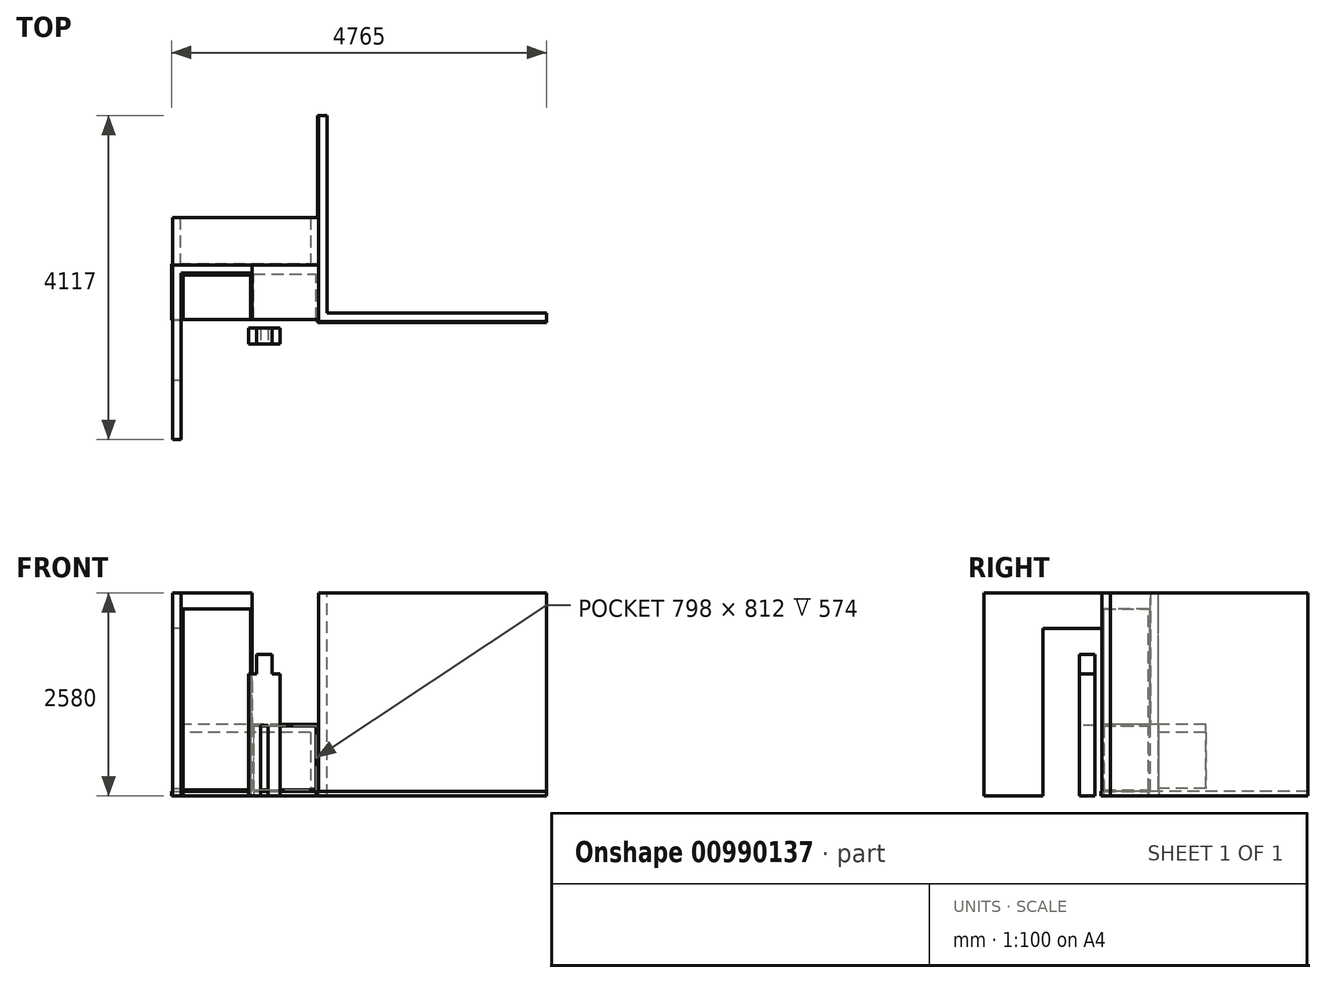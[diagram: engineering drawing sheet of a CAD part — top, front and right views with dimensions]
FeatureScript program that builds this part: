
annotation { "Feature Type Name" : "Feature", "Feature Type Description" : "" }
export const myFeature = defineFeature(function(context is Context, id is Id, definition is map)
    precondition{}
    {
        {
            assignVariable(context, id + "F0", {"name" : "mdf_espessura", "anyValue" : 18 * mm});
        }
        {
            assignVariable(context, id + "F1", {"name" : "porta_largura", "anyValue" : 775 * mm});
        }
        {
            assignVariable(context, id + "F2", {"name" : "parede_entrada_espessura", "anyValue" : 110 * mm});
        }
        {
            assignVariable(context, id + "F3", {"name" : "parede_entrada_largura", "anyValue" : 592 * mm});
        }
        {
            assignVariable(context, id + "F4", {"name" : "parede_janela_largura", "anyValue" : 1745 * mm});
        }
        {
            assignVariable(context, id + "F5", {"name" : "parede_lavanderia_largura", "anyValue" : 620 * mm});
        }
        {
            assignVariable(context, id + "F6", {"name" : "parede_geladeira_largura", "anyValue" : 750 * mm});
        }
        {
            var Q0;
            Q0=qCreatedBy(makeId("Front.planeOp"),FACE);
            var sketch = newSketch(context, id + "F7", { "sketchPlane" : qUnion([Q0])});
            skLineSegment(sketch, "E0.bottom", {"start": v(0, 0) * mm, "end": v(-110, 0) * mm});
            skLineSegment(sketch, "E0.top", {"start": v(0, 2580) * mm, "end": v(-110, 2580) * mm});
            skLineSegment(sketch, "E0.left", {"start": v(0, 0) * mm, "end": v(0, 2580) * mm});
            skLineSegment(sketch, "E0.right", {"start": v(-110, 0) * mm, "end": v(-110, 2580) * mm});
            skSolve(sketch);
        }
        {
            var Q0;
            Q0 = qSketchRegion(id + "F7", true);
            extrude(context, id + "F8", {"entities" : qUnion([Q0]), "depth" : getVariable(context, 'parede_entrada_largura'), "offsetDistance" : 25 * mm});
        }
        {
            var Q0;
            Q0=makeQuery(id+"F8.opExtrude","SWEPT_FACE",FACE,{"disambiguationData":[OSD([sQuery(id+"F7.wireOp",EDGE,"E0.left")])]});
            var sketch = newSketch(context, id + "F9", { "sketchPlane" : qUnion([Q0])});
            skLineSegment(sketch, "E1.bottom", {"start": v(0, 2580) * mm, "end": v(102, 2580) * mm});
            skLineSegment(sketch, "E1.top", {"start": v(0, 0) * mm, "end": v(102, 0) * mm});
            skLineSegment(sketch, "E1.left", {"start": v(0, 2580) * mm, "end": v(0, 0) * mm});
            skLineSegment(sketch, "E1.right", {"start": v(102, 2580) * mm, "end": v(102, 0) * mm});
            skSolve(sketch);
        }
        {
            var Q0;
            Q0 = qSketchRegion(id + "F9", true);
            var Q1;
            Q1=makeQuery(id+"F8.opExtrude","SWEPT_FACE",FACE,{"disambiguationData":[OSD([sQuery(id+"F7.wireOp",EDGE,"E0.right")])]});
            extrude(context, id + "F10", {"entities" : qUnion([Q0]), "operationType" : NewBodyOperationType.ADD, "depth" : getVariable(context, 'parede_janela_largura'), "offsetDistance" : 25 * mm, "hasSecondDirection" : true, "secondDirectionBound" : SecondDirectionBoundingType.UP_TO_SURFACE, "secondDirectionOppositeDirection" : true, "secondDirectionDepth" : 25 * mm, "secondDirectionBoundEntityFace" : qUnion([Q1])});
        }
        {
            var Q0;
            Q0=makeQuery(id+"F10.opExtrude","SWEPT_FACE",FACE,{"disambiguationData":[OSD([sQuery(id+"F9.wireOp",EDGE,"E1.left")])]});
            var sketch = newSketch(context, id + "F11", { "sketchPlane" : qUnion([Q0])});
            skLineSegment(sketch, "E2.bottom", {"start": v(1745, 2580) * mm, "end": v(901, 2580) * mm});
            skLineSegment(sketch, "E2.top", {"start": v(1745, 890) * mm, "end": v(901, 890) * mm});
            skLineSegment(sketch, "E2.left", {"start": v(1745, 2580) * mm, "end": v(1745, 890) * mm});
            skLineSegment(sketch, "E2.right", {"start": v(901, 2580) * mm, "end": v(901, 890) * mm});
            skSolve(sketch);
        }
        {
            var Q0;
            Q0 = qSketchRegion(id + "F11", true);
            extrude(context, id + "F12", {"entities" : qUnion([Q0]), "operationType" : NewBodyOperationType.REMOVE, "endBound" : BoundingType.THROUGH_ALL, "oppositeDirection" : true, "depth" : 25 * mm, "offsetDistance" : 25 * mm});
        }
        {
            var Q0;
            Q0=makeQuery(id+"F10.opExtrude","SWEPT_FACE",FACE,{"disambiguationData":[OSD([sQuery(id+"F9.wireOp",EDGE,"E1.left")])]});
            var sketch = newSketch(context, id + "F13", { "sketchPlane" : qUnion([Q0])});
            skLineSegment(sketch, "E3.bottom", {"start": v(1745, 0) * mm, "end": v(1855, 0) * mm});
            skLineSegment(sketch, "E3.top", {"start": v(1745, 2580) * mm, "end": v(1855, 2580) * mm});
            skLineSegment(sketch, "E3.left", {"start": v(1745, 0) * mm, "end": v(1745, 2580) * mm});
            skLineSegment(sketch, "E3.right", {"start": v(1855, 0) * mm, "end": v(1855, 2580) * mm});
            skSolve(sketch);
        }
        {
            var Q0;
            Q0 = qSketchRegion(id + "F13", true);
            var Q1;
            Q1=makeQuery(id+"F10.opExtrude","SWEPT_FACE",FACE,{"disambiguationData":[OSD([sQuery(id+"F9.wireOp",EDGE,"E1.right")])]});
            extrude(context, id + "F14", {"entities" : qUnion([Q0]), "operationType" : NewBodyOperationType.ADD, "depth" : getVariable(context, 'parede_lavanderia_largura'), "offsetDistance" : 25 * mm, "hasSecondDirection" : true, "secondDirectionOppositeDirection" : true, "secondDirectionDepth" : 2000 * mm, "secondDirectionBoundEntityFace" : qUnion([Q1])});
        }
        {
            var Q0;
            Q0=qCreatedBy(makeId("Top.planeOp"),FACE);
            var sketch = newSketch(context, id + "F15", { "sketchPlane" : qUnion([Q0])});
            skLineSegment(sketch, "E4.bottom", {"start": v(857.83, -903.42) * mm, "end": v(1257.83, -903.42) * mm});
            skLineSegment(sketch, "E4.top", {"start": v(857.83, -703.42) * mm, "end": v(1257.83, -703.42) * mm});
            skLineSegment(sketch, "E4.left", {"start": v(857.83, -903.42) * mm, "end": v(857.83, -703.42) * mm});
            skLineSegment(sketch, "E4.right", {"start": v(1257.83, -903.42) * mm, "end": v(1257.83, -703.42) * mm});
            skSolve(sketch);
        }
        {
            var Q0;
            Q0 = qSketchRegion(id + "F15", true);
            extrude(context, id + "F16", {"entities" : qUnion([Q0]), "depth" : 1550 * mm, "offsetDistance" : 25 * mm});
        }
        {
            var Q0;
            Q0=makeQuery(id+"F16.opExtrude","CAP_FACE",FACE,{"disambiguationData":[OSD([sQuery(id+"F15.wireOp",EDGE,"E4.bottom"),sQuery(id+"F15.wireOp",EDGE,"E4.top"),sQuery(id+"F15.wireOp",EDGE,"E4.left"),sQuery(id+"F15.wireOp",EDGE,"E4.right")])],"isStart":true});
            var sketch = newSketch(context, id + "F17", { "sketchPlane" : qUnion([Q0])});
            skLineSegment(sketch, "E5.bottom", {"start": v(1007.83, 703.42) * mm, "end": v(1107.83, 703.42) * mm});
            skLineSegment(sketch, "E5.top", {"start": v(1007.83, 903.42) * mm, "end": v(1107.83, 903.42) * mm});
            skLineSegment(sketch, "E5.left", {"start": v(1007.83, 703.42) * mm, "end": v(1007.83, 903.42) * mm});
            skLineSegment(sketch, "E5.right", {"start": v(1107.83, 703.42) * mm, "end": v(1107.83, 903.42) * mm});
            skSolve(sketch);
        }
        {
            var Q0;
            Q0 = qSketchRegion(id + "F17", true);
            extrude(context, id + "F18", {"entities" : qUnion([Q0]), "operationType" : NewBodyOperationType.REMOVE, "oppositeDirection" : true, "depth" : 900 * mm, "offsetDistance" : 25 * mm});
        }
        {
            var Q0;
            Q0=makeQuery(id+"F16.opExtrude","CAP_FACE",FACE,{"disambiguationData":[OSD([sQuery(id+"F15.wireOp",EDGE,"E4.bottom"),sQuery(id+"F15.wireOp",EDGE,"E4.top"),sQuery(id+"F15.wireOp",EDGE,"E4.left"),sQuery(id+"F15.wireOp",EDGE,"E4.right")])],"isStart":false});
            var sketch = newSketch(context, id + "F19", { "sketchPlane" : qUnion([Q0])});
            skLineSegment(sketch, "E6.bottom", {"start": v(957.83, -903.42) * mm, "end": v(1157.83, -903.42) * mm});
            skLineSegment(sketch, "E6.top", {"start": v(957.83, -703.42) * mm, "end": v(1157.83, -703.42) * mm});
            skLineSegment(sketch, "E6.left", {"start": v(957.83, -903.42) * mm, "end": v(957.83, -703.42) * mm});
            skLineSegment(sketch, "E6.right", {"start": v(1157.83, -903.42) * mm, "end": v(1157.83, -703.42) * mm});
            skSolve(sketch);
        }
        {
            var Q0;
            Q0 = qSketchRegion(id + "F19", true);
            extrude(context, id + "F20", {"entities" : qUnion([Q0]), "operationType" : NewBodyOperationType.ADD, "depth" : 250 * mm, "offsetDistance" : 25 * mm});
        }
        {
            var Q0;
            Q0=makeQuery(id+"F8.opExtrude","CAP_FACE",FACE,{"disambiguationData":[OSD([sQuery(id+"F7.wireOp",EDGE,"E0.bottom"),sQuery(id+"F7.wireOp",EDGE,"E0.top"),sQuery(id+"F7.wireOp",EDGE,"E0.left"),sQuery(id+"F7.wireOp",EDGE,"E0.right")])],"isStart":false});
            var sketch = newSketch(context, id + "F21", { "sketchPlane" : qUnion([Q0])});
            skLineSegment(sketch, "E7.bottom", {"start": v(0, 2580) * mm, "end": v(-110, 2580) * mm});
            skLineSegment(sketch, "E7.top", {"start": v(0, 2130) * mm, "end": v(-110, 2130) * mm});
            skLineSegment(sketch, "E7.left", {"start": v(0, 2580) * mm, "end": v(0, 2130) * mm});
            skLineSegment(sketch, "E7.right", {"start": v(-110, 2580) * mm, "end": v(-110, 2130) * mm});
            skSolve(sketch);
        }
        {
            var Q0;
            Q0 = qSketchRegion(id + "F21", true);
            extrude(context, id + "F22", {"entities" : qUnion([Q0]), "operationType" : NewBodyOperationType.ADD, "depth" : getVariable(context, 'porta_largura'), "offsetDistance" : 25 * mm});
        }
        {
            var Q0;
            Q0=makeQuery(id+"F22.opExtrude","CAP_FACE",FACE,{"disambiguationData":[OSD([sQuery(id+"F21.wireOp",EDGE,"E7.bottom"),sQuery(id+"F21.wireOp",EDGE,"E7.top"),sQuery(id+"F21.wireOp",EDGE,"E7.left"),sQuery(id+"F21.wireOp",EDGE,"E7.right")])],"isStart":false});
            var sketch = newSketch(context, id + "F23", { "sketchPlane" : qUnion([Q0])});
            skLineSegment(sketch, "E8.bottom", {"start": v(-110, 2580) * mm, "end": v(0, 2580) * mm});
            skLineSegment(sketch, "E8.top", {"start": v(-110, 0) * mm, "end": v(0, 0) * mm});
            skLineSegment(sketch, "E8.left", {"start": v(-110, 2580) * mm, "end": v(-110, 0) * mm});
            skLineSegment(sketch, "E8.right", {"start": v(0, 2580) * mm, "end": v(0, 0) * mm});
            skSolve(sketch);
        }
        {
            var Q0;
            Q0 = qSketchRegion(id + "F23", true);
            extrude(context, id + "F24", {"entities" : qUnion([Q0]), "operationType" : NewBodyOperationType.ADD, "depth" : getVariable(context, 'parede_geladeira_largura'), "offsetDistance" : 25 * mm});
        }
        {
            var Q0;
            Q0=makeQuery(id+"F14.opExtrude","CAP_FACE",FACE,{"disambiguationData":[OSD([sQuery(id+"F13.wireOp",EDGE,"E3.bottom"),sQuery(id+"F13.wireOp",EDGE,"E3.top"),sQuery(id+"F13.wireOp",EDGE,"E3.left"),sQuery(id+"F13.wireOp",EDGE,"E3.right")])],"isStart":false});
            var sketch = newSketch(context, id + "F25", { "sketchPlane" : qUnion([Q0])});
            skLineSegment(sketch, "E9.bottom", {"start": v(1855, 2580) * mm, "end": v(4645, 2580) * mm});
            skLineSegment(sketch, "E9.top", {"start": v(1855, 0) * mm, "end": v(4645, 0) * mm});
            skLineSegment(sketch, "E9.left", {"start": v(1855, 2580) * mm, "end": v(1855, 0) * mm});
            skLineSegment(sketch, "E9.right", {"start": v(4645, 2580) * mm, "end": v(4645, 0) * mm});
            skSolve(sketch);
        }
        {
            var Q0;
            Q0 = qSketchRegion(id + "F25", true);
            extrude(context, id + "F26", {"entities" : qUnion([Q0]), "operationType" : NewBodyOperationType.ADD, "oppositeDirection" : true, "depth" : getVariable(context, 'parede_entrada_espessura'), "offsetDistance" : 25 * mm});
        }
        {
            var Q0;
            Q0=makeQuery(id+"F24.boolean.opBoolean","MERGE",FACE,{"derivedFrom":[makeQuery(id+"F22.boolean.opBoolean","MERGE",FACE,{"derivedFrom":[makeQuery(id+"F8.opExtrude","SWEPT_FACE",FACE,{"disambiguationData":[OSD([sQuery(id+"F7.wireOp",EDGE,"E0.left")])]}),makeQuery(id+"F22.opExtrude","SWEPT_FACE",FACE,{"disambiguationData":[OSD([sQuery(id+"F21.wireOp",EDGE,"E7.left")])]})]}),makeQuery(id+"F24.opExtrude","SWEPT_FACE",FACE,{"disambiguationData":[OSD([sQuery(id+"F23.wireOp",EDGE,"E8.right")])]})]});
            var sketch = newSketch(context, id + "F27", { "sketchPlane" : qUnion([Q0])});
            skLineSegment(sketch, "E10.bottom", {"start": v(-2227, 2580) * mm, "end": v(-2117, 2580) * mm});
            skLineSegment(sketch, "E10.top", {"start": v(-2227, 0) * mm, "end": v(-2117, 0) * mm});
            skLineSegment(sketch, "E10.left", {"start": v(-2117, 2580) * mm, "end": v(-2117, 0) * mm});
            skLineSegment(sketch, "E10.right", {"start": v(-2227, 2580) * mm, "end": v(-2227, 0) * mm});
            skSolve(sketch);
        }
        {
            var Q0;
            Q0=makeQuery(id+"F8.opExtrude","CAP_FACE",FACE,{"disambiguationData":[OSD([sQuery(id+"F7.wireOp",EDGE,"E0.bottom"),sQuery(id+"F7.wireOp",EDGE,"E0.top"),sQuery(id+"F7.wireOp",EDGE,"E0.left"),sQuery(id+"F7.wireOp",EDGE,"E0.right")])],"isStart":false});
            var sketch = newSketch(context, id + "F28", { "sketchPlane" : qUnion([Q0])});
            skLineSegment(sketch, "E11.bottom", {"start": v(0, 0) * mm, "end": v(10, 0) * mm});
            skLineSegment(sketch, "E11.top", {"start": v(0, 60) * mm, "end": v(10, 60) * mm});
            skLineSegment(sketch, "E11.left", {"start": v(0, 0) * mm, "end": v(0, 60) * mm});
            skLineSegment(sketch, "E11.right", {"start": v(10, 0) * mm, "end": v(10, 60) * mm});
            skSolve(sketch);
        }
        {
            var Q0;
            Q0 = qSketchRegion(id + "F28", true);
            var Q1;
            Q1=makeQuery(id+"F8.opExtrude","CAP_EDGE",EDGE,{"disambiguationData":[OSD([sQuery(id+"F7.wireOp",EDGE,"E0.bottom")])],"isStart":false});
            var Q2;
            Q2=makeQuery(id+"F8.opExtrude","SWEPT_EDGE",EDGE,{"disambiguationData":[OSD([sQuery(id+"F7.wireOp",EDGE,"E0.bottom"),sQuery(id+"F7.wireOp",EDGE,"E0.left")])]});
            var Q3;
            Q3=makeQuery(id+"F10.opExtrude","SWEPT_EDGE",EDGE,{"disambiguationData":[OSD([sQuery(id+"F7.wireOp",EDGE,"E0.bottom"),sQuery(id+"F7.wireOp",EDGE,"E0.left"),sQuery(id+"F9.wireOp",EDGE,"E1.top"),sQuery(id+"F9.wireOp",EDGE,"E1.left")])]});
            var Q4;
            {var subQ0=sQuery(id+"F9.wireOp",EDGE,"E1.left");var subQ1=sQuery(id+"F13.wireOp",EDGE,"E3.bottom");var subQ2=sQuery(id+"F7.wireOp",EDGE,"E0.bottom");var subQ3=sQuery(id+"F9.wireOp",EDGE,"E1.top");var subQ4=sQuery(id+"F13.wireOp",EDGE,"E3.left");Q4=makeQuery(id+"F14.boolean.opBoolean","SPLIT",EDGE,{"disambiguationData":[TD([makeQuery(id+"F10.opExtrude","SWEPT_FACE",FACE,{"disambiguationData":[OSD([subQ0])]})])],"derivedFrom":makeQuery(id+"F14.opExtrude","SWEPT_EDGE",EDGE,{"disambiguationData":[OSD([subQ2,sQuery(id+"F7.wireOp",EDGE,"E0.left"),subQ3,subQ0,subQ1,subQ4])]})});}
            var Q5;
            Q5=makeQuery(id+"F26.boolean.opBoolean","MERGE",EDGE,{"derivedFrom":[makeQuery(id+"F14.opExtrude","CAP_EDGE",EDGE,{"disambiguationData":[OSD([sQuery(id+"F13.wireOp",EDGE,"E3.bottom")])],"isStart":false}),makeQuery(id+"F26.opExtrude","CAP_EDGE",EDGE,{"disambiguationData":[OSD([sQuery(id+"F25.wireOp",EDGE,"E9.top")])],"isStart":true})]});
            var Q6;
            Q6=makeQuery(id+"F10.boolean.opBoolean","MERGE",EDGE,{"derivedFrom":[makeQuery(id+"F8.opExtrude","SWEPT_EDGE",EDGE,{"disambiguationData":[OSD([sQuery(id+"F7.wireOp",EDGE,"E0.bottom"),sQuery(id+"F7.wireOp",EDGE,"E0.right")])]}),makeQuery(id+"F10.opExtrude","CAP_EDGE",EDGE,{"disambiguationData":[OSD([sQuery(id+"F9.wireOp",EDGE,"E1.top")])],"isStart":true})]});
            var Q7;
            Q7=makeQuery(id+"F10.opExtrude","SWEPT_EDGE",EDGE,{"disambiguationData":[OSD([sQuery(id+"F9.wireOp",EDGE,"E1.top"),sQuery(id+"F9.wireOp",EDGE,"E1.right")])]});
            var Q8;
            {var subQ0=sQuery(id+"F13.wireOp",EDGE,"E3.bottom");var subQ1=sQuery(id+"F7.wireOp",EDGE,"E0.bottom");var subQ2=sQuery(id+"F9.wireOp",EDGE,"E1.top");var subQ3=sQuery(id+"F13.wireOp",EDGE,"E3.left");Q8=makeQuery(id+"F14.boolean.opBoolean","SPLIT",EDGE,{"disambiguationData":[TD([makeQuery(id+"F10.opExtrude","SWEPT_FACE",FACE,{"disambiguationData":[OSD([sQuery(id+"F9.wireOp",EDGE,"E1.right")])]})])],"derivedFrom":makeQuery(id+"F14.opExtrude","SWEPT_EDGE",EDGE,{"disambiguationData":[OSD([subQ1,sQuery(id+"F7.wireOp",EDGE,"E0.left"),subQ2,sQuery(id+"F9.wireOp",EDGE,"E1.left"),subQ0,subQ3])]})});}
            sweep(context, id + "F29", {"profiles" : qUnion([Q0]), "path" : qUnion([Q1, Q2, Q3, Q4, Q5, Q6, Q7, Q8])});
        }
        {
            var Q0;
            Q0=makeQuery(id+"F29.opSweep","SWEPT_FACE",FACE,{"disambiguationData":[OSD([sQuery(id+"F7.wireOp",EDGE,"E0.bottom"),sQuery(id+"F7.wireOp",EDGE,"E0.left"),sQuery(id+"F28.wireOp",EDGE,"E11.right")])]});
            var sketch = newSketch(context, id + "F30", { "sketchPlane" : qUnion([Q0])});
            skLineSegment(sketch, "E12.bottom", {"start": v(-10, 0) * mm, "end": v(-592, 0) * mm});
            skLineSegment(sketch, "E12.top", {"start": v(-10, 2380) * mm, "end": v(-592, 2380) * mm});
            skLineSegment(sketch, "E12.left", {"start": v(-10, 0) * mm, "end": v(-10, 2380) * mm});
            skLineSegment(sketch, "E12.right", {"start": v(-592, 0) * mm, "end": v(-592, 2380) * mm});
            skSolve(sketch);
        }
        {
            var Q0;
            Q0 = qSketchRegion(id + "F30", true);
            extrude(context, id + "F31", {"entities" : qUnion([Q0]), "depth" : getVariable(context, 'mdf_espessura'), "offsetDistance" : 25 * mm});
        }
        {
            var Q0;
            Q0=makeQuery(id+"F29.opSweep","SWEPT_FACE",FACE,{"disambiguationData":[OSD([sQuery(id+"F7.wireOp",EDGE,"E0.bottom"),sQuery(id+"F7.wireOp",EDGE,"E0.left"),sQuery(id+"F9.wireOp",EDGE,"E1.top"),sQuery(id+"F9.wireOp",EDGE,"E1.left"),sQuery(id+"F28.wireOp",EDGE,"E11.right")])]});
            var sketch = newSketch(context, id + "F32", { "sketchPlane" : qUnion([Q0])});
            skLineSegment(sketch, "E13.bottom", {"start": v(28, 0) * mm, "end": v(901, 0) * mm});
            skLineSegment(sketch, "E13.top", {"start": v(28, 2380) * mm, "end": v(901, 2380) * mm});
            skLineSegment(sketch, "E13.left", {"start": v(28, 0) * mm, "end": v(28, 2380) * mm});
            skLineSegment(sketch, "E13.right", {"start": v(901, 0) * mm, "end": v(901, 2380) * mm});
            skSolve(sketch);
        }
        {
            var Q0;
            Q0 = qSketchRegion(id + "F32", true);
            extrude(context, id + "F33", {"entities" : qUnion([Q0]), "operationType" : NewBodyOperationType.ADD, "depth" : getVariable(context, 'mdf_espessura'), "offsetDistance" : 25 * mm});
        }
        {
            var Q0;
            Q0=makeQuery(id+"F33.opExtrude","CAP_FACE",FACE,{"disambiguationData":[OSD([sQuery(id+"F32.wireOp",EDGE,"E13.bottom"),sQuery(id+"F32.wireOp",EDGE,"E13.top"),sQuery(id+"F32.wireOp",EDGE,"E13.left"),sQuery(id+"F32.wireOp",EDGE,"E13.right")])],"isStart":false});
            var sketch = newSketch(context, id + "F34", { "sketchPlane" : qUnion([Q0])});
            skLineSegment(sketch, "E14.bottom", {"start": v(901, 2380) * mm, "end": v(883, 2380) * mm});
            skLineSegment(sketch, "E14.top", {"start": v(901, 0) * mm, "end": v(883, 0) * mm});
            skLineSegment(sketch, "E14.left", {"start": v(901, 2380) * mm, "end": v(901, 0) * mm});
            skLineSegment(sketch, "E14.right", {"start": v(883, 2380) * mm, "end": v(883, 0) * mm});
            skSolve(sketch);
        }
        {
            var Q0;
            Q0 = qSketchRegion(id + "F34", true);
            var Q1;
            Q1=makeQuery(id+"F31.opExtrude","SWEPT_FACE",FACE,{"disambiguationData":[OSD([sQuery(id+"F30.wireOp",EDGE,"E12.right")])]});
            extrude(context, id + "F35", {"entities" : qUnion([Q0]), "operationType" : NewBodyOperationType.ADD, "endBound" : BoundingType.UP_TO_SURFACE, "depth" : 25 * mm, "endBoundEntityFace" : qUnion([Q1]), "offsetDistance" : 25 * mm});
        }
        {
            var Q0;
            Q0=makeQuery(id+"F33.opExtrude","CAP_FACE",FACE,{"disambiguationData":[OSD([sQuery(id+"F32.wireOp",EDGE,"E13.bottom"),sQuery(id+"F32.wireOp",EDGE,"E13.top"),sQuery(id+"F32.wireOp",EDGE,"E13.left"),sQuery(id+"F32.wireOp",EDGE,"E13.right")])],"isStart":false});
            var sketch = newSketch(context, id + "F36", { "sketchPlane" : qUnion([Q0])});
            skLineSegment(sketch, "E15.bottom", {"start": v(28, 60) * mm, "end": v(883, 60) * mm});
            skLineSegment(sketch, "E15.top", {"start": v(28, 78) * mm, "end": v(883, 78) * mm});
            skLineSegment(sketch, "E15.left", {"start": v(28, 60) * mm, "end": v(28, 78) * mm});
            skLineSegment(sketch, "E15.right", {"start": v(883, 60) * mm, "end": v(883, 78) * mm});
            skSolve(sketch);
        }
        {
            var Q0;
            Q0 = qSketchRegion(id + "F36", true);
            var Q1;
            Q1=makeQuery(id+"F31.opExtrude","SWEPT_FACE",FACE,{"disambiguationData":[OSD([sQuery(id+"F30.wireOp",EDGE,"E12.right")])]});
            extrude(context, id + "F37", {"entities" : qUnion([Q0]), "operationType" : NewBodyOperationType.ADD, "endBound" : BoundingType.UP_TO_SURFACE, "depth" : 25 * mm, "endBoundEntityFace" : qUnion([Q1]), "offsetDistance" : 25 * mm});
        }
        {
            var Q0;
            Q0=makeQuery(id+"F10.opExtrude","SWEPT_FACE",FACE,{"disambiguationData":[OSD([sQuery(id+"F9.wireOp",EDGE,"E1.left")])]});
            var sketch = newSketch(context, id + "F38", { "sketchPlane" : qUnion([Q0])});
            skLineSegment(sketch, "E16.bottom", {"start": v(901, 0) * mm, "end": v(1735, 0) * mm});
            skLineSegment(sketch, "E16.top", {"start": v(901, 890) * mm, "end": v(1735, 890) * mm});
            skLineSegment(sketch, "E16.left", {"start": v(901, 0) * mm, "end": v(901, 890) * mm});
            skLineSegment(sketch, "E16.right", {"start": v(1735, 0) * mm, "end": v(1735, 890) * mm});
            skSolve(sketch);
        }
        {
            var Q0;
            Q0 = qSketchRegion(id + "F38", true);
            extrude(context, id + "F39", {"entities" : qUnion([Q0]), "depth" : getVariable(context, 'mdf_espessura'), "offsetDistance" : 25 * mm});
        }
        {
            var Q0;
            Q0=makeQuery(id+"F39.opExtrude","CAP_FACE",FACE,{"disambiguationData":[OSD([sQuery(id+"F38.wireOp",EDGE,"E16.bottom"),sQuery(id+"F38.wireOp",EDGE,"E16.top"),sQuery(id+"F38.wireOp",EDGE,"E16.left"),sQuery(id+"F38.wireOp",EDGE,"E16.right")])],"isStart":false});
            var sketch = newSketch(context, id + "F40", { "sketchPlane" : qUnion([Q0])});
            skLineSegment(sketch, "E17.bottom", {"start": v(901, 890) * mm, "end": v(919, 890) * mm});
            skLineSegment(sketch, "E17.top", {"start": v(901, 0) * mm, "end": v(919, 0) * mm});
            skLineSegment(sketch, "E17.left", {"start": v(901, 890) * mm, "end": v(901, 0) * mm});
            skLineSegment(sketch, "E17.right", {"start": v(919, 890) * mm, "end": v(919, 0) * mm});
            skLineSegment(sketch, "E18.bottom", {"start": v(1735, 0) * mm, "end": v(1717, 0) * mm});
            skLineSegment(sketch, "E18.top", {"start": v(1735, 890) * mm, "end": v(1717, 890) * mm});
            skLineSegment(sketch, "E18.left", {"start": v(1735, 0) * mm, "end": v(1735, 890) * mm});
            skLineSegment(sketch, "E18.right", {"start": v(1717, 0) * mm, "end": v(1717, 890) * mm});
            skSolve(sketch);
        }
        {
            var Q0;
            Q0 = qSketchRegion(id + "F40", true);
            var Q1;
            Q1=makeQuery(id+"F37.boolean.opBoolean","MERGE",FACE,{"derivedFrom":[makeQuery(id+"F31.opExtrude","SWEPT_FACE",FACE,{"disambiguationData":[OSD([sQuery(id+"F30.wireOp",EDGE,"E12.right")])]}),makeQuery(id+"F35.opExtrude","CAP_FACE",FACE,{"disambiguationData":[OSD([sQuery(id+"F34.wireOp",EDGE,"E14.bottom"),sQuery(id+"F34.wireOp",EDGE,"E14.top"),sQuery(id+"F34.wireOp",EDGE,"E14.left"),sQuery(id+"F34.wireOp",EDGE,"E14.right")])],"isStart":false}),makeQuery(id+"F37.opExtrude","CAP_FACE",FACE,{"disambiguationData":[OSD([sQuery(id+"F36.wireOp",EDGE,"E15.bottom"),sQuery(id+"F36.wireOp",EDGE,"E15.top"),sQuery(id+"F36.wireOp",EDGE,"E15.left"),sQuery(id+"F36.wireOp",EDGE,"E15.right")])],"isStart":false})]});
            extrude(context, id + "F41", {"entities" : qUnion([Q0]), "operationType" : NewBodyOperationType.ADD, "endBound" : BoundingType.UP_TO_SURFACE, "depth" : 25 * mm, "endBoundEntityFace" : qUnion([Q1]), "offsetDistance" : 25 * mm});
        }
        {
            var Q0;
            Q0=makeQuery(id+"F12.boolean.opBoolean","COPY",FACE,{"derivedFrom":makeQuery(id+"F12.opExtrude","SWEPT_FACE",FACE,{"disambiguationData":[OSD([sQuery(id+"F11.wireOp",EDGE,"E2.top")])]})});
            var sketch = newSketch(context, id + "F42", { "sketchPlane" : qUnion([Q0])});
            skLineSegment(sketch, "E19.bottom", {"start": v(901, 102) * mm, "end": v(1745, 102) * mm});
            skLineSegment(sketch, "E19.top", {"start": v(901, -592) * mm, "end": v(1745, -592) * mm});
            skLineSegment(sketch, "E19.left", {"start": v(901, 102) * mm, "end": v(901, -592) * mm});
            skLineSegment(sketch, "E19.right", {"start": v(1745, 102) * mm, "end": v(1745, -592) * mm});
            skSolve(sketch);
        }
        {
            var Q0;
            Q0 = qSketchRegion(id + "F42", true);
            extrude(context, id + "F43", {"entities" : qUnion([Q0]), "operationType" : NewBodyOperationType.ADD, "depth" : getVariable(context, 'mdf_espessura'), "offsetDistance" : 25 * mm});
        }
        {
            var Q0;
            Q0=makeQuery(id+"F39.opExtrude","CAP_FACE",FACE,{"disambiguationData":[OSD([sQuery(id+"F38.wireOp",EDGE,"E16.bottom"),sQuery(id+"F38.wireOp",EDGE,"E16.top"),sQuery(id+"F38.wireOp",EDGE,"E16.left"),sQuery(id+"F38.wireOp",EDGE,"E16.right")])],"isStart":false});
            var sketch = newSketch(context, id + "F44", { "sketchPlane" : qUnion([Q0])});
            skLineSegment(sketch, "E20.bottom", {"start": v(919, 60) * mm, "end": v(1717, 60) * mm});
            skLineSegment(sketch, "E20.top", {"start": v(919, 78) * mm, "end": v(1717, 78) * mm});
            skLineSegment(sketch, "E20.left", {"start": v(919, 60) * mm, "end": v(919, 78) * mm});
            skLineSegment(sketch, "E20.right", {"start": v(1717, 60) * mm, "end": v(1717, 78) * mm});
            skSolve(sketch);
        }
        {
            var Q0;
            Q0 = qSketchRegion(id + "F44", true);
            var Q1;
            Q1=makeQuery(id+"F43.boolean.opBoolean","MERGE",FACE,{"derivedFrom":[makeQuery(id+"F41.opExtrude","CAP_FACE",FACE,{"disambiguationData":[OSD([sQuery(id+"F40.wireOp",EDGE,"E17.bottom"),sQuery(id+"F40.wireOp",EDGE,"E17.top"),sQuery(id+"F40.wireOp",EDGE,"E17.left"),sQuery(id+"F40.wireOp",EDGE,"E17.right")])],"isStart":false}),makeQuery(id+"F41.opExtrude","CAP_FACE",FACE,{"disambiguationData":[OSD([sQuery(id+"F40.wireOp",EDGE,"E18.bottom"),sQuery(id+"F40.wireOp",EDGE,"E18.top"),sQuery(id+"F40.wireOp",EDGE,"E18.left"),sQuery(id+"F40.wireOp",EDGE,"E18.right")])],"isStart":false}),makeQuery(id+"F43.opExtrude","SWEPT_FACE",FACE,{"disambiguationData":[OSD([sQuery(id+"F42.wireOp",EDGE,"E19.top")])]})]});
            extrude(context, id + "F45", {"entities" : qUnion([Q0]), "operationType" : NewBodyOperationType.ADD, "endBound" : BoundingType.UP_TO_SURFACE, "depth" : 25 * mm, "endBoundEntityFace" : qUnion([Q1]), "offsetDistance" : 25 * mm});
        }
        {
            var Q0;
            Q0=makeQuery(id+"F10.opExtrude","SWEPT_FACE",FACE,{"disambiguationData":[OSD([sQuery(id+"F9.wireOp",EDGE,"E1.right")])]});
            var sketch = newSketch(context, id + "F46", { "sketchPlane" : qUnion([Q0])});
            skLineSegment(sketch, "E21.bottom", {"start": v(-1745, 908) * mm, "end": v(110, 908) * mm});
            skLineSegment(sketch, "E21.top", {"start": v(-1745, 808) * mm, "end": v(110, 808) * mm});
            skLineSegment(sketch, "E21.left", {"start": v(-1745, 908) * mm, "end": v(-1745, 808) * mm});
            skLineSegment(sketch, "E21.right", {"start": v(110, 908) * mm, "end": v(110, 808) * mm});
            skLineSegment(sketch, "E22.bottom", {"start": v(110, 808) * mm, "end": v(10, 808) * mm});
            skLineSegment(sketch, "E22.top", {"start": v(110, 100) * mm, "end": v(10, 100) * mm});
            skLineSegment(sketch, "E22.left", {"start": v(110, 808) * mm, "end": v(110, 100) * mm});
            skLineSegment(sketch, "E22.right", {"start": v(10, 808) * mm, "end": v(10, 100) * mm});
            skLineSegment(sketch, "E23.bottom", {"start": v(-1745, 808) * mm, "end": v(-1645, 808) * mm});
            skLineSegment(sketch, "E23.top", {"start": v(-1745, 100) * mm, "end": v(-1645, 100) * mm});
            skLineSegment(sketch, "E23.left", {"start": v(-1745, 808) * mm, "end": v(-1745, 100) * mm});
            skLineSegment(sketch, "E23.right", {"start": v(-1645, 808) * mm, "end": v(-1645, 100) * mm});
            skSolve(sketch);
        }
        {
            var Q0;
            Q0 = qSketchRegion(id + "F46", true);
            extrude(context, id + "F47", {"entities" : qUnion([Q0]), "depth" : 600 * mm, "offsetDistance" : 25 * mm});
        }
    });
